# Revit family: QF_Vollrath 72009_72522
name_source: partatom
category: Specialty Equipment
revit_build: Autodesk Revit 2016 (Build: 20151007_0715(x64)
units: mm (PartAtom-declared; Revit-internal decimal feet)

## family parameters
Always vertical = Yes
Cut with Voids When Loaded = No
OmniClass Number = 23.40.40.11.31
OmniClass Title = Steam Tables
Part Type = Normal
Room Calculation Point = No
Round Connector Dimension = Use Diameter
Shared = No
Work Plane-Based = No

## types (2) — shared parameters
Assembly Code = E1090320
CSI MasterFormat = 11 42 13
Depth = 12.63 "
Description = Merchandiser, Heat 'N Serve
Elec Conn Connection Height = 2 "
Height = 9.63 "
Manufacturer = Vollrath
Phase = 1
URL = www.vollrathco.com
Watts = 800 W
Weight in Pounds = 11.3
Width = 12.63 "

## per-type parameters (varying)
| type | Apparent Power | Conn Plug | Cycle | FL Amps | Volts |
| 72009 | 804 VA | NEMA 5-15P | 60 Hz | 7 A | 120 V |
| 72522 | 805 VA | SCHUKO | 50 Hz | 4 A | 230 V |

note: column(s) folded — value = type name in every type: Model

## geometry (parser evidence)
native form markers: Blend x18, Sweep x3
no freeform markers — native parametric forms only
